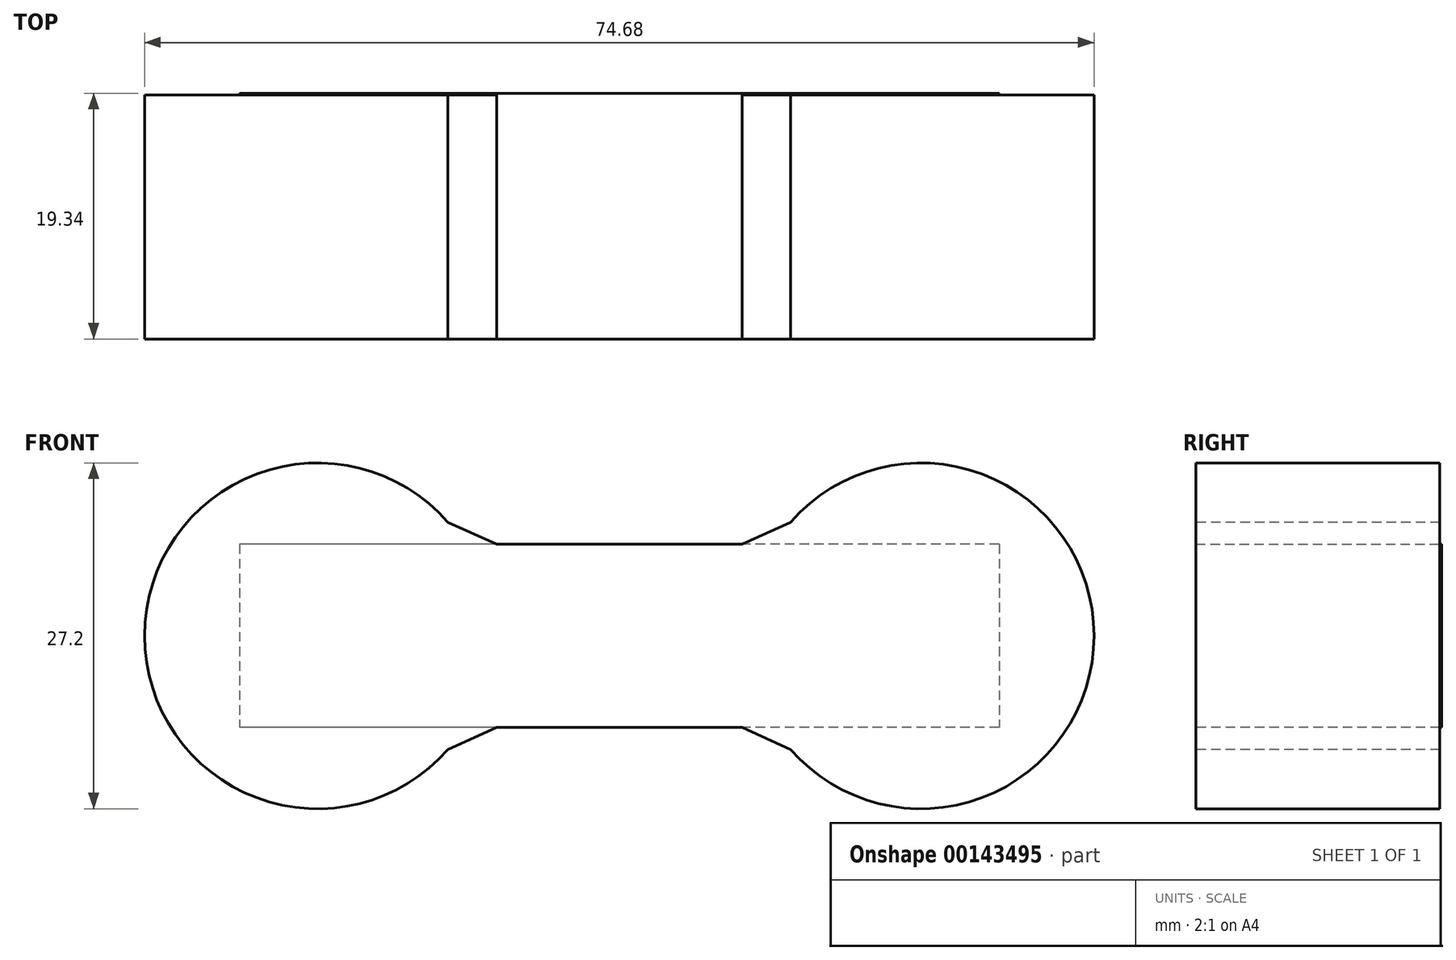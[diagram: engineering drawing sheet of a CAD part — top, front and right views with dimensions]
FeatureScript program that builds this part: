
annotation { "Feature Type Name" : "Feature", "Feature Type Description" : "" }
export const myFeature = defineFeature(function(context is Context, id is Id, definition is map)
    precondition{}
    {
        {
            var Q0;
            Q0=qCreatedBy(makeId("Front.planeOp"),FACE);
            var sketch = newSketch(context, id + "F0", { "sketchPlane" : qUnion([Q0])});
            skLineSegment(sketch, "E0.bottom", {"start": v(29.87, 7.2) * mm, "end": v(-29.87, 7.2) * mm});
            skLineSegment(sketch, "E0.top", {"start": v(29.87, -7.2) * mm, "end": v(-29.87, -7.2) * mm});
            skLineSegment(sketch, "E0.left", {"start": v(29.87, 7.2) * mm, "end": v(29.87, -7.2) * mm});
            skLineSegment(sketch, "E0.right", {"start": v(-29.87, 7.2) * mm, "end": v(-29.87, -7.2) * mm});
            skPoint(sketch, "E0.middle", {"position": v(0, 0) * mm});
            skSolve(sketch);
        }
        {
            var Q0;
            Q0 = qSketchRegion(id + "F0", true);
            extrude(context, id + "F1", {"entities" : qUnion([Q0]), "endBound" : BoundingType.SYMMETRIC, "depth" : 19.34 * mm});
        }
        {
            var Q0;
            Q0=makeQuery(id+"F1.opExtrude","CAP_FACE",FACE,{"disambiguationData":[OSD([sQuery(id+"F0.wireOp",EDGE,"E0.bottom"),sQuery(id+"F0.wireOp",EDGE,"E0.top"),sQuery(id+"F0.wireOp",EDGE,"E0.left"),sQuery(id+"F0.wireOp",EDGE,"E0.right")])],"isStart":false});
            var sketch = newSketch(context, id + "F2", { "sketchPlane" : qUnion([Q0])});
            skCircle(sketch, "E1", {"center": v(-23.74, 0) * mm, "radius": 13.6 * mm});
            skCircle(sketch, "E2.MirrorC", {"center": v(23.74, 0) * mm, "radius": 13.6 * mm});
            skSolve(sketch);
        }
        {
            var Q0;
            Q0 = qSketchRegion(id + "F2", true);
            extrude(context, id + "F3", {"entities" : qUnion([Q0]), "operationType" : NewBodyOperationType.ADD, "oppositeDirection" : true, "depth" : 19.2 * mm});
        }
        {
            var Q0;
            Q0=makeQuery(id+"F3.boolean.opBoolean","INTERSECT",EDGE,{"derivedFrom":[makeQuery(id+"F1.opExtrude","SWEPT_FACE",FACE,{"disambiguationData":[OSD([sQuery(id+"F0.wireOp",EDGE,"E0.bottom")])]}),makeQuery(id+"F3.opExtrude","SWEPT_FACE",FACE,{"disambiguationData":[OSD([sQuery(id+"F2.wireOp",EDGE,"E2.MirrorC")])]})]});
            var Q1;
            Q1=makeQuery(id+"F3.boolean.opBoolean","INTERSECT",EDGE,{"derivedFrom":[makeQuery(id+"F1.opExtrude","SWEPT_FACE",FACE,{"disambiguationData":[OSD([sQuery(id+"F0.wireOp",EDGE,"E0.bottom")])]}),makeQuery(id+"F3.opExtrude","SWEPT_FACE",FACE,{"disambiguationData":[OSD([sQuery(id+"F2.wireOp",EDGE,"E1")])]})]});
            var Q2;
            Q2=makeQuery(id+"F3.boolean.opBoolean","INTERSECT",EDGE,{"derivedFrom":[makeQuery(id+"F1.opExtrude","SWEPT_FACE",FACE,{"disambiguationData":[OSD([sQuery(id+"F0.wireOp",EDGE,"E0.top")])]}),makeQuery(id+"F3.opExtrude","SWEPT_FACE",FACE,{"disambiguationData":[OSD([sQuery(id+"F2.wireOp",EDGE,"E2.MirrorC")])]})]});
            var Q3;
            Q3=makeQuery(id+"F3.boolean.opBoolean","INTERSECT",EDGE,{"derivedFrom":[makeQuery(id+"F1.opExtrude","SWEPT_FACE",FACE,{"disambiguationData":[OSD([sQuery(id+"F0.wireOp",EDGE,"E0.top")])]}),makeQuery(id+"F3.opExtrude","SWEPT_FACE",FACE,{"disambiguationData":[OSD([sQuery(id+"F2.wireOp",EDGE,"E1")])]})]});
            chamfer(context, id + "F4", {"entities" : qUnion([Q0, Q1, Q2, Q3]), "width" : 5.08 * mm, "tangentPropagation" : true});
        }
    });
